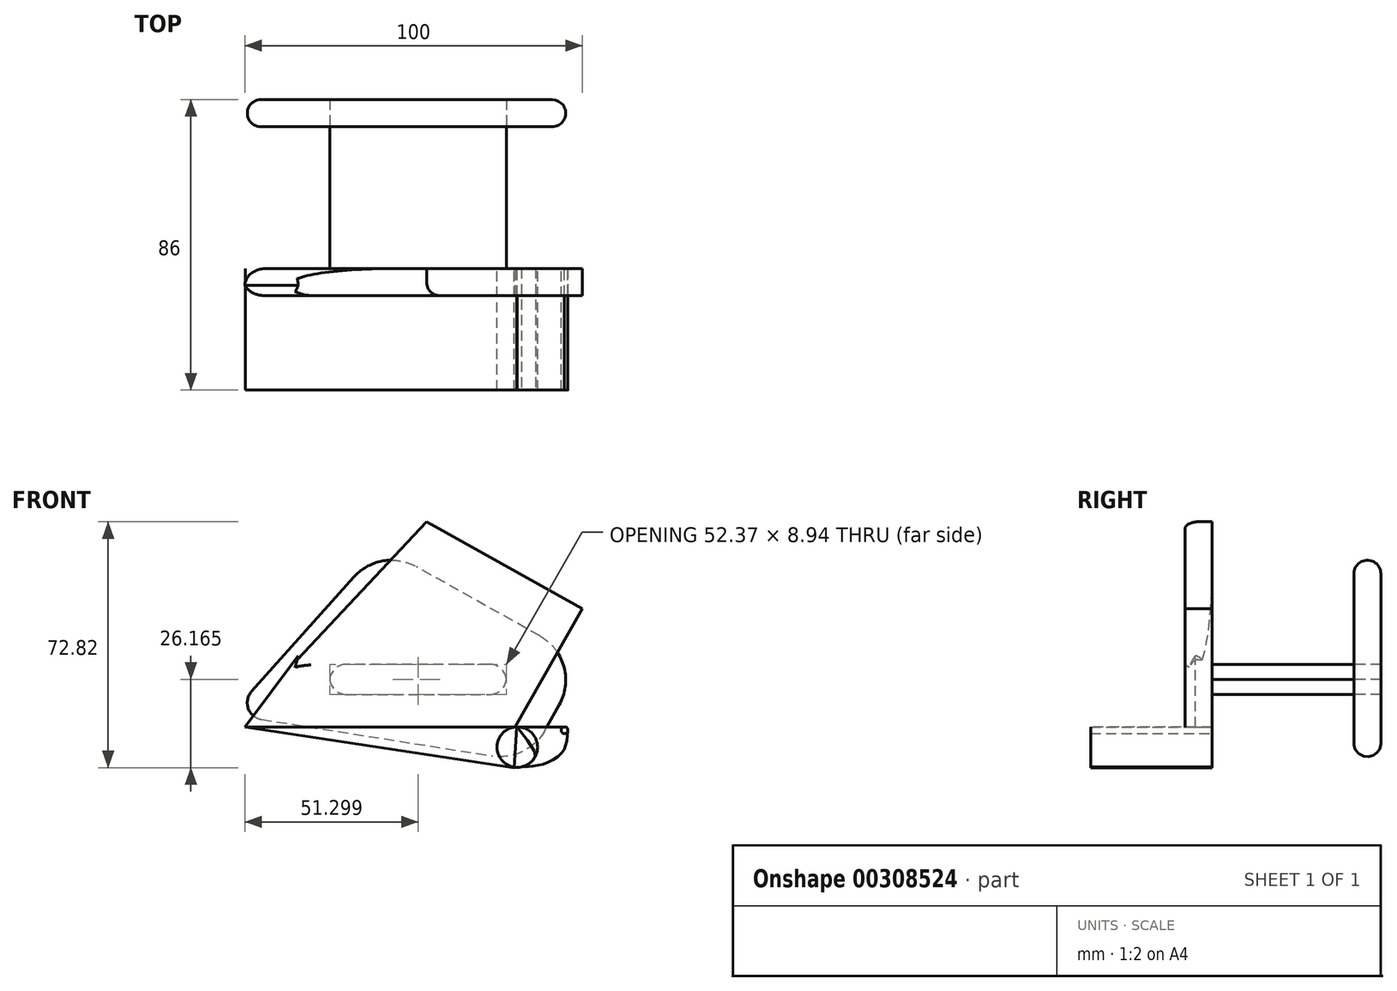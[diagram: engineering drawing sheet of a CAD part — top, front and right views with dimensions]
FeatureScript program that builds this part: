
annotation { "Feature Type Name" : "Feature", "Feature Type Description" : "" }
export const myFeature = defineFeature(function(context is Context, id is Id, definition is map)
    precondition{}
    {
        {
            var Q0;
            Q0=qCreatedBy(makeId("Front.planeOp"),FACE);
            var sketch = newSketch(context, id + "F0", { "sketchPlane" : qUnion([Q0])});
            skLineSegment(sketch, "E0", {"start": v(-52.1, 0) * mm, "end": v(-52.1, -15.97) * mm, "construction": true});
            skLineSegment(sketch, "E1", {"start": v(47.9, 0.4) * mm, "end": v(47.9, -14.17) * mm, "construction": true});
            skLineSegment(sketch, "E2", {"start": v(-52.1, 0) * mm, "end": v(57.49, 0) * mm, "construction": true});
            skLineSegment(sketch, "E3", {"start": v(-40.32, -12) * mm, "end": v(53.96, -12) * mm, "construction": true});
            skLineSegment(sketch, "E4", {"start": v(-52.1, 0) * mm, "end": v(-52.1, 54.96) * mm, "construction": true});
            skLineSegment(sketch, "E5", {"start": v(-4.1, 64) * mm, "end": v(-4.1, 4.82) * mm, "construction": true});
            skLineSegment(sketch, "E6", {"start": v(47.9, 0.4) * mm, "end": v(47.9, 65.26) * mm, "construction": true});
            skLineSegment(sketch, "E7", {"start": v(27.9, 7.78) * mm, "end": v(27.9, -18.09) * mm, "construction": true});
            skLineSegment(sketch, "E8", {"start": v(35.94, 35) * mm, "end": v(61.58, 35) * mm, "construction": true});
            skLineSegment(sketch, "E9", {"start": v(-52.1, 0) * mm, "end": v(-4.1, 64) * mm});
            skLineSegment(sketch, "E10", {"start": v(-4.1, 64) * mm, "end": v(47.9, 35) * mm});
            skLineSegment(sketch, "E11", {"start": v(47.9, 35) * mm, "end": v(27.9, 0) * mm});
            skLineSegment(sketch, "E12", {"start": v(27.9, 0) * mm, "end": v(-52.1, 0) * mm});
            skLineSegment(sketch, "E13", {"start": v(19.09, -6) * mm, "end": v(56.41, -6) * mm, "construction": true});
            skLineSegment(sketch, "E14", {"start": v(41.9, 6.08) * mm, "end": v(41.9, -18.4) * mm, "construction": true});
            skPoint(sketch, "E15", {"position": v(41.9, -6) * mm});
            skCircle(sketch, "E16", {"center": v(41.9, -6) * mm, "radius": 6 * mm});
            skLineSegment(sketch, "E17", {"start": v(-52.1, 0) * mm, "end": v(41.14, -11.95) * mm});
            skLineSegment(sketch, "E18", {"start": v(-52.1, 0) * mm, "end": v(41.9, 0) * mm});
            skSolve(sketch);
        }
        {
            var Q0;
            {var subQ0=sQuery(id+"F0.wireOp",EDGE,"E17");Q0=makeQuery(id+"F0.imprint","IMPRINT",FACE,{"disambiguationData":[TD([[makeQuery(id+"F0.imprint","IMPRINT",EDGE,{"derivedFrom":subQ0}),1.0]])]});}
            var Q1;
            {var subQ0=sQuery(id+"F0.wireOp",EDGE,"E16");var subQ1=makeQuery(id+"F0.imprint","INTERSECT",VERTEX,{"derivedFrom":[subQ0,sQuery(id+"F0.wireOp",EDGE,"E17")]});Q1=makeQuery(id+"F0.imprint","IMPRINT",FACE,{"disambiguationData":[TD([[makeQuery(id+"F0.imprint","IMPRINT",EDGE,{"disambiguationData":[TD([[subQ1,1.0]])],"derivedFrom":subQ0}),1.0]])]});}
            extrude(context, id + "F1", {"entities" : qUnion([Q0, Q1]), "depth" : 35 * mm});
        }
        {
            var Q0;
            Q0=qSketchRegion(id+"F0",true);
            extrude(context, id + "F2", {"entities" : qUnion([Q0]), "operationType" : NewBodyOperationType.ADD, "depth" : 8 * mm});
        }
        {
            var Q0;
            Q0=qCreatedBy(makeId("Front.planeOp"),FACE);
            var sketch = newSketch(context, id + "F3", { "sketchPlane" : qUnion([Q0])});
            skLineSegment(sketch, "E19", {"start": v(-36.63, 19.92) * mm, "end": v(9.84, 69.36) * mm});
            skLineSegment(sketch, "E20", {"start": v(9.84, 69.36) * mm, "end": v(-23.58, 69.36) * mm});
            skLineSegment(sketch, "E21", {"start": v(-23.58, 69.36) * mm, "end": v(-36.63, 19.92) * mm});
            skSolve(sketch);
        }
        {
            var Q0;
            Q0=qSketchRegion(id+"F3",true);
            extrude(context, id + "F4", {"entities" : qUnion([Q0]), "operationType" : NewBodyOperationType.REMOVE, "depth" : 25 * mm});
        }
        {
            var Q0;
            {var subQ0=sQuery(id+"FbqoypqFBOhr57J_1.wireOp",EDGE,"BRQSndQV-g5sf-zvzY-DvSG-huqyq08V7I3I");var subQ1=sQuery(id+"F0.wireOp",EDGE,"E11");var subQ2=sQuery(id+"F0.wireOp",EDGE,"E10");var subQ3=sQuery(id+"FbqoypqFBOhr57J_1.wireOp",EDGE,"8b525e8e-8c6c-4e49-b2c8-9a34a7f034ca.0");var subQ4=sQuery(id+"F0.wireOp",EDGE,"E18");var subQ5=sQuery(id+"F0.wireOp",EDGE,"E17");var subQ6=sQuery(id+"F0.wireOp",EDGE,"E16");var subQ7=sQuery(id+"F0.wireOp",EDGE,"E9");Q0=makeQuery(id+"F4.boolean.opBoolean","INTERSECT",EDGE,{"derivedFrom":[makeQuery(id+"FkfvDilHx9DTRUl_1.boolean.opBoolean","SPLIT",FACE,{"disambiguationData":[TD([makeQuery(id+"F2.opExtrude","SWEPT_FACE",FACE,{"disambiguationData":[OSD([subQ2])]})])],"derivedFrom":makeQuery(id+"Fdf2VJ1HoHcF5vq_1.boolean.opBoolean","MERGE",FACE,{"derivedFrom":[makeQuery(id+"F2.opExtrude","CAP_FACE",FACE,{"disambiguationData":[OSD([subQ7,subQ2,subQ1,subQ6,subQ5,subQ4])],"isStart":false}),makeQuery(id+"Fdf2VJ1HoHcF5vq_1.opExtrude","SWEPT_FACE",FACE,{"disambiguationData":[OSD([subQ7,subQ2,subQ1,subQ6,subQ5,subQ4,subQ0,subQ3])]})]})}),makeQuery(id+"F4.opExtrude","SWEPT_FACE",FACE,{"disambiguationData":[OSD([sQuery(id+"F3.wireOp",EDGE,"E19")])]})]});}
            var Q1;
            Q1=makeQuery(id+"F4.boolean.opBoolean","COPY",EDGE,{"derivedFrom":makeQuery(id+"F4.opExtrude","CAP_EDGE",EDGE,{"disambiguationData":[OSD([sQuery(id+"F3.wireOp",EDGE,"E19")])],"isStart":true})});
            fillet(context, id + "F5", {"entities" : qUnion([Q0, Q1]), "radius" : 4 * mm, "tangentPropagation" : true, "allowEdgeOverflow" : false});
        }
        {
            var Q0;
            Q0=makeQuery(id+"F2.opExtrude","CAP_EDGE",EDGE,{"disambiguationData":[OSD([sQuery(id+"F0.wireOp",EDGE,"E9")])],"isStart":true});
            fillet(context, id + "F6", {"entities" : qUnion([Q0]), "radius" : 5 * mm, "tangentPropagation" : true, "allowEdgeOverflow" : false});
        }
        {
            var Q0;
            {var subQ0=sQuery(id+"FbqoypqFBOhr57J_1.wireOp",EDGE,"8b525e8e-8c6c-4e49-b2c8-9a34a7f034ca.0");var subQ1=sQuery(id+"FbqoypqFBOhr57J_1.wireOp",EDGE,"BRQSndQV-g5sf-zvzY-DvSG-huqyq08V7I3I");var subQ2=sQuery(id+"F0.wireOp",EDGE,"E18");var subQ3=sQuery(id+"F0.wireOp",EDGE,"E17");var subQ4=sQuery(id+"F0.wireOp",EDGE,"E16");var subQ7=makeQuery(id+"F1.opExtrude","CAP_FACE",FACE,{"disambiguationData":[OSD([subQ4,subQ3,subQ2])],"isStart":false});Q0=makeQuery(id+"Fdf2VJ1HoHcF5vq_1.boolean.opBoolean","MERGE",FACE,{"derivedFrom":[makeQuery(id+"F4MmlgvdSOgh8WJ_1.boolean.opBoolean","SPLIT",FACE,{"disambiguationData":[TD([makeQuery(id+"F4MmlgvdSOgh8WJ_1.opExtrude","CAP_FACE",FACE,{"disambiguationData":[OSD([subQ1,subQ0])],"isStart":true})])],"derivedFrom":subQ7}),makeQuery(id+"F4MmlgvdSOgh8WJ_1.boolean.opBoolean","SPLIT",FACE,{"disambiguationData":[TD([makeQuery(id+"F1.opExtrude","SWEPT_FACE",FACE,{"disambiguationData":[OSD([subQ4])]})])],"derivedFrom":subQ7}),makeQuery(id+"Fdf2VJ1HoHcF5vq_1.opExtrude","SWEPT_FACE",FACE,{"disambiguationData":[OSD([subQ4,subQ3,subQ2,subQ1,subQ0])]})]});}
            extrude(context, id + "F7", {"entities" : qUnion([Q0]), "operationType" : NewBodyOperationType.REMOVE, "oppositeDirection" : true, "depth" : 35 * mm});
        }
        {
            var Q0;
            Q0=qCreatedBy(makeId("Front.planeOp"),FACE);
            var sketch = newSketch(context, id + "F8", { "sketchPlane" : qUnion([Q0])});
            skLineSegment(sketch, "E22", {"start": v(-56.4, 4.13) * mm, "end": v(-56.4, -20.87) * mm, "construction": true});
            skLineSegment(sketch, "E23", {"start": v(43.6, 4.62) * mm, "end": v(43.6, -14.93) * mm, "construction": true});
            skLineSegment(sketch, "E24", {"start": v(-61.12, -12) * mm, "end": v(48.3, -12) * mm, "construction": true});
            skLineSegment(sketch, "E25", {"start": v(-61.12, 0) * mm, "end": v(48.07, 0) * mm, "construction": true});
            skLineSegment(sketch, "E26", {"start": v(15.3, -6) * mm, "end": v(48.15, -6) * mm, "construction": true});
            skLineSegment(sketch, "E27", {"start": v(28.6, 2.35) * mm, "end": v(28.6, -16.77) * mm, "construction": true});
            skPoint(sketch, "E28", {"position": v(28.6, -6) * mm});
            skCircle(sketch, "E29", {"center": v(28.6, -6) * mm, "radius": 6 * mm});
            skLineSegment(sketch, "E30", {"start": v(42.6, 2.12) * mm, "end": v(42.6, -4.76) * mm, "construction": true});
            skLineSegment(sketch, "E31", {"start": v(39.06, -1) * mm, "end": v(45.23, -1) * mm, "construction": true});
            skPoint(sketch, "E32", {"position": v(42.6, -1) * mm});
            skCircle(sketch, "E33", {"center": v(42.6, -1) * mm, "radius": 1 * mm});
            skSolve(sketch);
        }
        {
            var Q0;
            Q0=makeQuery(id+"F8.imprint","IMPRINT",FACE,{"disambiguationData":[TD([[makeQuery(id+"F8.imprint","IMPRINT",EDGE,{"derivedFrom":sQuery(id+"F8.wireOp",EDGE,"E33")}),1.0]])]});
            var Q1;
            Q1=makeQuery(id+"F8.imprint","IMPRINT",FACE,{"disambiguationData":[TD([[makeQuery(id+"F8.imprint","IMPRINT",EDGE,{"derivedFrom":sQuery(id+"F8.wireOp",EDGE,"E29")}),1.0]])]});
            extrude(context, id + "F9", {"entities" : qUnion([Q0, Q1]), "depth" : 36 * mm});
        }
        {
            var Q0;
            Q0=qCreatedBy(makeId("Front.planeOp"),FACE);
            var sketch = newSketch(context, id + "F10", { "sketchPlane" : qUnion([Q0])});
            skFitSpline(sketch, "E34", {"points": [v(28.58, 0) * mm, v(42.55, 0) * mm], "startDerivative": vector(13.97, 0) * mm, "endDerivative": vector(13.97, 0) * mm});
            skFitSpline(sketch, "E35", {"points": [v(42.55, 0) * mm, v(42.75, 0) * mm, v(42.97, 0) * mm, v(43.19, -0.17) * mm, v(43.34, -0.32) * mm, v(43.5, -0.53) * mm, v(43.58, -0.8) * mm, v(43.58, -1.02) * mm, v(43.55, -1.3) * mm, v(43.4, -3.3) * mm, v(43.3, -4.42) * mm, v(42.9, -5.55) * mm, v(42.55, -6.61) * mm, v(41.8, -7.62) * mm, v(40.7, -8.7) * mm, v(39.2, -9.76) * mm, v(37.47, -10.6) * mm, v(35.83, -11.14) * mm, v(34.32, -11.4) * mm, v(32.7, -11.64) * mm, v(29.82, -11.83) * mm, v(31.21, -11.4) * mm, v(32.13, -10.85) * mm, v(32.8, -10.22) * mm, v(33.33, -9.7) * mm, v(33.76, -8.97) * mm, v(34.08, -8.3) * mm, v(28.58, 0) * mm], "startDerivative": vector(12.22, -0.6) * mm, "endDerivative": vector(-72.88, 95.43) * mm});
            skSolve(sketch);
        }
        {
            var Q0;
            Q0=qSketchRegion(id+"F10",true);
            extrude(context, id + "F11", {"entities" : qUnion([Q0]), "depth" : 36 * mm});
        }
        {
            var Q0;
            Q0=qCreatedBy(makeId("Front.planeOp"),FACE);
            var sketch = newSketch(context, id + "F12", { "sketchPlane" : qUnion([Q0])});
            skLineSegment(sketch, "E36", {"start": v(28.47, 0) * mm, "end": v(27.7, -12.08) * mm});
            skLineSegment(sketch, "E37", {"start": v(27.7, -12.08) * mm, "end": v(-51.96, 0) * mm});
            skLineSegment(sketch, "E38", {"start": v(-51.96, 0) * mm, "end": v(28.47, 0) * mm});
            skSolve(sketch);
        }
        {
            var Q0;
            Q0=makeQuery(id+"F12.imprint","IMPRINT",FACE,{"disambiguationData":[TD([[makeQuery(id+"F12.imprint","IMPRINT",EDGE,{"derivedFrom":sQuery(id+"F12.wireOp",EDGE,"E36")}),-1.0]])]});
            extrude(context, id + "F13", {"entities" : qUnion([Q0]), "depth" : 36 * mm});
        }
        {
            var Q0;
            Q0=qCreatedBy(makeId("Front.planeOp"),FACE);
            var sketch = newSketch(context, id + "F14", { "sketchPlane" : qUnion([Q0])});
            skLineSegment(sketch, "E39", {"start": v(25.41, 18.55) * mm, "end": v(-27.01, 18.55) * mm});
            skLineSegment(sketch, "E40", {"start": v(-27.01, 18.55) * mm, "end": v(-27.01, 9.61) * mm});
            skLineSegment(sketch, "E41", {"start": v(-27.01, 9.61) * mm, "end": v(25.41, 9.61) * mm});
            skLineSegment(sketch, "E42", {"start": v(25.41, 9.61) * mm, "end": v(25.41, 18.55) * mm});
            skSolve(sketch);
        }
        {
            var Q0;
            Q0 = qSketchRegion(id + "F14", true);
            extrude(context, id + "F15", {"entities" : qUnion([Q0]), "oppositeDirection" : true, "depth" : 42 * mm});
        }
        {
            var Q0;
            Q0=makeQuery(id+"F15.opExtrude","SWEPT_EDGE",EDGE,{"disambiguationData":[OSD([sQuery(id+"F14.wireOp",EDGE,"E39"),sQuery(id+"F14.wireOp",EDGE,"E42")])]});
            var Q1;
            Q1=makeQuery(id+"F15.opExtrude","SWEPT_EDGE",EDGE,{"disambiguationData":[OSD([sQuery(id+"F14.wireOp",EDGE,"E41"),sQuery(id+"F14.wireOp",EDGE,"E42")])]});
            var Q2;
            Q2=makeQuery(id+"F15.opExtrude","SWEPT_EDGE",EDGE,{"disambiguationData":[OSD([sQuery(id+"F14.wireOp",EDGE,"E40"),sQuery(id+"F14.wireOp",EDGE,"E41")])]});
            var Q3;
            Q3=makeQuery(id+"F15.opExtrude","SWEPT_EDGE",EDGE,{"disambiguationData":[OSD([sQuery(id+"F14.wireOp",EDGE,"E39"),sQuery(id+"F14.wireOp",EDGE,"E40")])]});
            fillet(context, id + "F16", {"entities" : qUnion([Q0, Q1, Q2, Q3]), "radius" : 5 * mm, "tangentPropagation" : true, "allowEdgeOverflow" : false});
        }
        {
            var Q0;
            Q0=makeQuery(id+"F2.opExtrude","CAP_EDGE",EDGE,{"disambiguationData":[OSD([sQuery(id+"F0.wireOp",EDGE,"E9")])],"isStart":false});
            fillet(context, id + "F17", {"entities" : qUnion([Q0]), "radius" : 5 * mm, "tangentPropagation" : true, "allowEdgeOverflow" : false});
        }
        {
            var Q0;
            Q0=makeQuery(id+"F15.opExtrude","CAP_FACE",FACE,{"disambiguationData":[OSD([sQuery(id+"F14.wireOp",EDGE,"E39"),sQuery(id+"F14.wireOp",EDGE,"E40"),sQuery(id+"F14.wireOp",EDGE,"E41"),sQuery(id+"F14.wireOp",EDGE,"E42")])],"isStart":false});
            var sketch = newSketch(context, id + "F18", { "sketchPlane" : qUnion([Q0])});
            skLineSegment(sketch, "E43", {"start": v(0, 46.7) * mm, "end": v(-48.35, 19.6) * mm});
            skLineSegment(sketch, "E44", {"start": v(-48.35, 19.6) * mm, "end": v(-31.61, -10.25) * mm});
            skLineSegment(sketch, "E45", {"start": v(-31.61, -10.25) * mm, "end": v(56.25, 3.66) * mm});
            skLineSegment(sketch, "E46", {"start": v(56.25, 3.66) * mm, "end": v(11.83, 53.33) * mm});
            skLineSegment(sketch, "E47", {"start": v(-4.93, 43.94) * mm, "end": v(11.83, 53.33) * mm});
            skSolve(sketch);
        }
        {
            var Q0;
            {var subQ6=sQuery(id+"F18.wireOp",EDGE,"E43");Q0=makeQuery(id+"F18.imprint","IMPRINT",FACE,{"disambiguationData":[TD([[makeQuery(id+"F18.imprint","IMPRINT",EDGE,{"derivedFrom":subQ6}),1.0]])]});}
            extrude(context, id + "F19", {"entities" : qUnion([Q0]), "depth" : 8 * mm});
        }
        {
            var Q0;
            Q0=makeQuery(id+"F15.opExtrude","CAP_FACE",FACE,{"disambiguationData":[OSD([sQuery(id+"F14.wireOp",EDGE,"E39"),sQuery(id+"F14.wireOp",EDGE,"E40"),sQuery(id+"F14.wireOp",EDGE,"E41"),sQuery(id+"F14.wireOp",EDGE,"E42")])],"isStart":false});
            extrude(context, id + "F20", {"entities" : qUnion([Q0]), "depth" : 8 * mm});
        }
        {
            var Q0;
            Q0=makeQuery(id+"F19.opExtrude","SWEPT_EDGE",EDGE,{"disambiguationData":[OSD([sQuery(id+"F18.wireOp",EDGE,"E43"),sQuery(id+"F18.wireOp",EDGE,"E44")])]});
            var Q1;
            Q1=makeQuery(id+"F19.opExtrude","SWEPT_EDGE",EDGE,{"disambiguationData":[OSD([sQuery(id+"F18.wireOp",EDGE,"E44"),sQuery(id+"F18.wireOp",EDGE,"E45")])]});
            var Q2;
            Q2=makeQuery(id+"F19.opExtrude","SWEPT_EDGE",EDGE,{"disambiguationData":[OSD([sQuery(id+"F18.wireOp",EDGE,"E46"),sQuery(id+"F18.wireOp",EDGE,"E47")])]});
            fillet(context, id + "F21", {"entities" : qUnion([Q0, Q1, Q2]), "radius" : 15 * mm, "tangentPropagation" : true, "allowEdgeOverflow" : false});
        }
        {
            var Q0;
            Q0=makeQuery(id+"F19.opExtrude","SWEPT_EDGE",EDGE,{"disambiguationData":[OSD([sQuery(id+"F18.wireOp",EDGE,"E45"),sQuery(id+"F18.wireOp",EDGE,"E46")])]});
            fillet(context, id + "F22", {"entities" : qUnion([Q0]), "radius" : 5 * mm, "tangentPropagation" : true, "allowEdgeOverflow" : false});
        }
        {
            var Q0;
            Q0=makeQuery(id+"F19.opExtrude","CAP_EDGE",EDGE,{"disambiguationData":[OSD([sQuery(id+"F18.wireOp",EDGE,"E45")])],"isStart":false});
            var Q1;
            {var subQ0=sQuery(id+"F18.wireOp",EDGE,"E45");var subQ1=sQuery(id+"F18.wireOp",EDGE,"E44");Q1=makeQuery(id+"F21.opFillet","BLEND_EDGE",EDGE,{"blendedFrom":[makeQuery(id+"F19.opExtrude","SWEPT_EDGE",EDGE,{"disambiguationData":[OSD([subQ1,subQ0])]}),makeQuery(id+"F19.opExtrude","CAP_FACE",FACE,{"disambiguationData":[OSD([sQuery(id+"F14.wireOp",EDGE,"E39"),sQuery(id+"F14.wireOp",EDGE,"E40"),sQuery(id+"F14.wireOp",EDGE,"E41"),sQuery(id+"F14.wireOp",EDGE,"E42"),sQuery(id+"F18.wireOp",EDGE,"E43"),subQ1,subQ0,sQuery(id+"F18.wireOp",EDGE,"E46"),sQuery(id+"F18.wireOp",EDGE,"E47")])],"isStart":false})],"blendedInto":[makeQuery(id+"F19.opExtrude","CAP_FACE",FACE,{"disambiguationData":[OSD([sQuery(id+"F14.wireOp",EDGE,"E39"),sQuery(id+"F14.wireOp",EDGE,"E40"),sQuery(id+"F14.wireOp",EDGE,"E41"),sQuery(id+"F14.wireOp",EDGE,"E42"),sQuery(id+"F18.wireOp",EDGE,"E43"),subQ1,subQ0,sQuery(id+"F18.wireOp",EDGE,"E46"),sQuery(id+"F18.wireOp",EDGE,"E47")])],"isStart":false})]});}
            var Q2;
            Q2=makeQuery(id+"F19.opExtrude","CAP_EDGE",EDGE,{"disambiguationData":[OSD([sQuery(id+"F18.wireOp",EDGE,"E44")])],"isStart":false});
            var Q3;
            {var subQ0=sQuery(id+"F18.wireOp",EDGE,"E44");var subQ1=sQuery(id+"F18.wireOp",EDGE,"E43");Q3=makeQuery(id+"F21.opFillet","BLEND_EDGE",EDGE,{"blendedFrom":[makeQuery(id+"F19.opExtrude","SWEPT_EDGE",EDGE,{"disambiguationData":[OSD([subQ1,subQ0])]}),makeQuery(id+"F19.opExtrude","CAP_FACE",FACE,{"disambiguationData":[OSD([sQuery(id+"F14.wireOp",EDGE,"E39"),sQuery(id+"F14.wireOp",EDGE,"E40"),sQuery(id+"F14.wireOp",EDGE,"E41"),sQuery(id+"F14.wireOp",EDGE,"E42"),subQ1,subQ0,sQuery(id+"F18.wireOp",EDGE,"E45"),sQuery(id+"F18.wireOp",EDGE,"E46"),sQuery(id+"F18.wireOp",EDGE,"E47")])],"isStart":false})],"blendedInto":[makeQuery(id+"F19.opExtrude","CAP_FACE",FACE,{"disambiguationData":[OSD([sQuery(id+"F14.wireOp",EDGE,"E39"),sQuery(id+"F14.wireOp",EDGE,"E40"),sQuery(id+"F14.wireOp",EDGE,"E41"),sQuery(id+"F14.wireOp",EDGE,"E42"),subQ1,subQ0,sQuery(id+"F18.wireOp",EDGE,"E45"),sQuery(id+"F18.wireOp",EDGE,"E46"),sQuery(id+"F18.wireOp",EDGE,"E47")])],"isStart":false})]});}
            var Q4;
            Q4=makeQuery(id+"F19.opExtrude","CAP_EDGE",EDGE,{"disambiguationData":[OSD([sQuery(id+"F18.wireOp",EDGE,"E43"),sQuery(id+"F18.wireOp",EDGE,"E47")])],"isStart":false});
            var Q5;
            {var subQ0=sQuery(id+"F18.wireOp",EDGE,"E47");var subQ1=sQuery(id+"F18.wireOp",EDGE,"E46");Q5=makeQuery(id+"F21.opFillet","BLEND_EDGE",EDGE,{"blendedFrom":[makeQuery(id+"F19.opExtrude","SWEPT_EDGE",EDGE,{"disambiguationData":[OSD([subQ1,subQ0])]}),makeQuery(id+"F19.opExtrude","CAP_FACE",FACE,{"disambiguationData":[OSD([sQuery(id+"F14.wireOp",EDGE,"E39"),sQuery(id+"F14.wireOp",EDGE,"E40"),sQuery(id+"F14.wireOp",EDGE,"E41"),sQuery(id+"F14.wireOp",EDGE,"E42"),sQuery(id+"F18.wireOp",EDGE,"E43"),sQuery(id+"F18.wireOp",EDGE,"E44"),sQuery(id+"F18.wireOp",EDGE,"E45"),subQ1,subQ0])],"isStart":false})],"blendedInto":[makeQuery(id+"F19.opExtrude","CAP_FACE",FACE,{"disambiguationData":[OSD([sQuery(id+"F14.wireOp",EDGE,"E39"),sQuery(id+"F14.wireOp",EDGE,"E40"),sQuery(id+"F14.wireOp",EDGE,"E41"),sQuery(id+"F14.wireOp",EDGE,"E42"),sQuery(id+"F18.wireOp",EDGE,"E43"),sQuery(id+"F18.wireOp",EDGE,"E44"),sQuery(id+"F18.wireOp",EDGE,"E45"),subQ1,subQ0])],"isStart":false})]});}
            var Q6;
            Q6=makeQuery(id+"F19.opExtrude","CAP_EDGE",EDGE,{"disambiguationData":[OSD([sQuery(id+"F18.wireOp",EDGE,"E46")])],"isStart":false});
            var Q7;
            {var subQ0=sQuery(id+"F18.wireOp",EDGE,"E46");var subQ1=sQuery(id+"F18.wireOp",EDGE,"E45");Q7=makeQuery(id+"F22.opFillet","BLEND_EDGE",EDGE,{"blendedFrom":[makeQuery(id+"F19.opExtrude","SWEPT_EDGE",EDGE,{"disambiguationData":[OSD([subQ1,subQ0])]}),makeQuery(id+"F19.opExtrude","CAP_FACE",FACE,{"disambiguationData":[OSD([sQuery(id+"F14.wireOp",EDGE,"E39"),sQuery(id+"F14.wireOp",EDGE,"E40"),sQuery(id+"F14.wireOp",EDGE,"E41"),sQuery(id+"F14.wireOp",EDGE,"E42"),sQuery(id+"F18.wireOp",EDGE,"E43"),sQuery(id+"F18.wireOp",EDGE,"E44"),subQ1,subQ0,sQuery(id+"F18.wireOp",EDGE,"E47")])],"isStart":false})],"blendedInto":[makeQuery(id+"F19.opExtrude","CAP_FACE",FACE,{"disambiguationData":[OSD([sQuery(id+"F14.wireOp",EDGE,"E39"),sQuery(id+"F14.wireOp",EDGE,"E40"),sQuery(id+"F14.wireOp",EDGE,"E41"),sQuery(id+"F14.wireOp",EDGE,"E42"),sQuery(id+"F18.wireOp",EDGE,"E43"),sQuery(id+"F18.wireOp",EDGE,"E44"),subQ1,subQ0,sQuery(id+"F18.wireOp",EDGE,"E47")])],"isStart":false})]});}
            fillet(context, id + "F23", {"entities" : qUnion([Q0, Q1, Q2, Q3, Q4, Q5, Q6, Q7]), "radius" : 4 * mm, "tangentPropagation" : true, "allowEdgeOverflow" : false});
        }
        {
            var Q0;
            Q0=makeQuery(id+"F19.opExtrude","CAP_EDGE",EDGE,{"disambiguationData":[OSD([sQuery(id+"F18.wireOp",EDGE,"E46")])],"isStart":true});
            var Q1;
            {var subQ0=sQuery(id+"F18.wireOp",EDGE,"E47");var subQ1=sQuery(id+"F18.wireOp",EDGE,"E46");Q1=makeQuery(id+"F21.opFillet","BLEND_EDGE",EDGE,{"blendedFrom":[makeQuery(id+"F19.opExtrude","SWEPT_EDGE",EDGE,{"disambiguationData":[OSD([subQ1,subQ0])]}),makeQuery(id+"F19.opExtrude","CAP_FACE",FACE,{"disambiguationData":[OSD([sQuery(id+"F14.wireOp",EDGE,"E39"),sQuery(id+"F14.wireOp",EDGE,"E40"),sQuery(id+"F14.wireOp",EDGE,"E41"),sQuery(id+"F14.wireOp",EDGE,"E42"),sQuery(id+"F18.wireOp",EDGE,"E43"),sQuery(id+"F18.wireOp",EDGE,"E44"),sQuery(id+"F18.wireOp",EDGE,"E45"),subQ1,subQ0])],"isStart":true})],"blendedInto":[makeQuery(id+"F19.opExtrude","CAP_FACE",FACE,{"disambiguationData":[OSD([sQuery(id+"F14.wireOp",EDGE,"E39"),sQuery(id+"F14.wireOp",EDGE,"E40"),sQuery(id+"F14.wireOp",EDGE,"E41"),sQuery(id+"F14.wireOp",EDGE,"E42"),sQuery(id+"F18.wireOp",EDGE,"E43"),sQuery(id+"F18.wireOp",EDGE,"E44"),sQuery(id+"F18.wireOp",EDGE,"E45"),subQ1,subQ0])],"isStart":true})]});}
            var Q2;
            Q2=makeQuery(id+"F19.opExtrude","CAP_EDGE",EDGE,{"disambiguationData":[OSD([sQuery(id+"F18.wireOp",EDGE,"E43"),sQuery(id+"F18.wireOp",EDGE,"E47")])],"isStart":true});
            var Q3;
            {var subQ0=sQuery(id+"F18.wireOp",EDGE,"E44");var subQ1=sQuery(id+"F18.wireOp",EDGE,"E43");Q3=makeQuery(id+"F21.opFillet","BLEND_EDGE",EDGE,{"blendedFrom":[makeQuery(id+"F19.opExtrude","SWEPT_EDGE",EDGE,{"disambiguationData":[OSD([subQ1,subQ0])]}),makeQuery(id+"F19.opExtrude","CAP_FACE",FACE,{"disambiguationData":[OSD([sQuery(id+"F14.wireOp",EDGE,"E39"),sQuery(id+"F14.wireOp",EDGE,"E40"),sQuery(id+"F14.wireOp",EDGE,"E41"),sQuery(id+"F14.wireOp",EDGE,"E42"),subQ1,subQ0,sQuery(id+"F18.wireOp",EDGE,"E45"),sQuery(id+"F18.wireOp",EDGE,"E46"),sQuery(id+"F18.wireOp",EDGE,"E47")])],"isStart":true})],"blendedInto":[makeQuery(id+"F19.opExtrude","CAP_FACE",FACE,{"disambiguationData":[OSD([sQuery(id+"F14.wireOp",EDGE,"E39"),sQuery(id+"F14.wireOp",EDGE,"E40"),sQuery(id+"F14.wireOp",EDGE,"E41"),sQuery(id+"F14.wireOp",EDGE,"E42"),subQ1,subQ0,sQuery(id+"F18.wireOp",EDGE,"E45"),sQuery(id+"F18.wireOp",EDGE,"E46"),sQuery(id+"F18.wireOp",EDGE,"E47")])],"isStart":true})]});}
            var Q4;
            Q4=makeQuery(id+"F19.opExtrude","CAP_EDGE",EDGE,{"disambiguationData":[OSD([sQuery(id+"F18.wireOp",EDGE,"E44")])],"isStart":true});
            var Q5;
            {var subQ0=sQuery(id+"F18.wireOp",EDGE,"E45");var subQ1=sQuery(id+"F18.wireOp",EDGE,"E44");Q5=makeQuery(id+"F21.opFillet","BLEND_EDGE",EDGE,{"blendedFrom":[makeQuery(id+"F19.opExtrude","SWEPT_EDGE",EDGE,{"disambiguationData":[OSD([subQ1,subQ0])]}),makeQuery(id+"F19.opExtrude","CAP_FACE",FACE,{"disambiguationData":[OSD([sQuery(id+"F14.wireOp",EDGE,"E39"),sQuery(id+"F14.wireOp",EDGE,"E40"),sQuery(id+"F14.wireOp",EDGE,"E41"),sQuery(id+"F14.wireOp",EDGE,"E42"),sQuery(id+"F18.wireOp",EDGE,"E43"),subQ1,subQ0,sQuery(id+"F18.wireOp",EDGE,"E46"),sQuery(id+"F18.wireOp",EDGE,"E47")])],"isStart":true})],"blendedInto":[makeQuery(id+"F19.opExtrude","CAP_FACE",FACE,{"disambiguationData":[OSD([sQuery(id+"F14.wireOp",EDGE,"E39"),sQuery(id+"F14.wireOp",EDGE,"E40"),sQuery(id+"F14.wireOp",EDGE,"E41"),sQuery(id+"F14.wireOp",EDGE,"E42"),sQuery(id+"F18.wireOp",EDGE,"E43"),subQ1,subQ0,sQuery(id+"F18.wireOp",EDGE,"E46"),sQuery(id+"F18.wireOp",EDGE,"E47")])],"isStart":true})]});}
            var Q6;
            Q6=makeQuery(id+"F19.opExtrude","CAP_EDGE",EDGE,{"disambiguationData":[OSD([sQuery(id+"F18.wireOp",EDGE,"E45")])],"isStart":true});
            var Q7;
            {var subQ0=sQuery(id+"F18.wireOp",EDGE,"E46");var subQ1=sQuery(id+"F18.wireOp",EDGE,"E45");Q7=makeQuery(id+"F22.opFillet","BLEND_EDGE",EDGE,{"blendedFrom":[makeQuery(id+"F19.opExtrude","SWEPT_EDGE",EDGE,{"disambiguationData":[OSD([subQ1,subQ0])]}),makeQuery(id+"F19.opExtrude","CAP_FACE",FACE,{"disambiguationData":[OSD([sQuery(id+"F14.wireOp",EDGE,"E39"),sQuery(id+"F14.wireOp",EDGE,"E40"),sQuery(id+"F14.wireOp",EDGE,"E41"),sQuery(id+"F14.wireOp",EDGE,"E42"),sQuery(id+"F18.wireOp",EDGE,"E43"),sQuery(id+"F18.wireOp",EDGE,"E44"),subQ1,subQ0,sQuery(id+"F18.wireOp",EDGE,"E47")])],"isStart":true})],"blendedInto":[makeQuery(id+"F19.opExtrude","CAP_FACE",FACE,{"disambiguationData":[OSD([sQuery(id+"F14.wireOp",EDGE,"E39"),sQuery(id+"F14.wireOp",EDGE,"E40"),sQuery(id+"F14.wireOp",EDGE,"E41"),sQuery(id+"F14.wireOp",EDGE,"E42"),sQuery(id+"F18.wireOp",EDGE,"E43"),sQuery(id+"F18.wireOp",EDGE,"E44"),subQ1,subQ0,sQuery(id+"F18.wireOp",EDGE,"E47")])],"isStart":true})]});}
            fillet(context, id + "F24", {"entities" : qUnion([Q0, Q1, Q2, Q3, Q4, Q5, Q6, Q7]), "radius" : 4 * mm, "tangentPropagation" : true, "allowEdgeOverflow" : false});
        }
    });
